# Revit family: Tub_Spout-American_Standard-Townsend_S-888809X_Series
name_source: partatom
category: Plumbing Fixtures
units: mm (PartAtom-declared; Revit-internal decimal feet)

## family parameters
Cut with Voids When Loaded = No
Host = Face
OmniClass Number = 23.45.05.14.21
OmniClass Title = Bathtubs
Part Type = Normal
Room Calculation Point = No
Round Connector Dimension = Use Diameter
Shared = Yes

## types (9) — shared parameters
Assembly Code = D2020300
CW Connection = No
CWFU = 3
Default Elevation = 25"
HW Connection = No
HWFU = 3
Height = 2 5/8"
Installation Type = Wall Mounted
Length = 6 1/2"
Manufacturer = American Standard
Product Documentation Link = https://americanstandard.box.com
Product Page URL = https://www.americanstandard-us.com
Tempered Water Connection = Yes
Tempered Water Connection Diameter = 1/2"
URL = https://www.americanstandard-us.com
Vent Connection = No
WFU = 4
Warranty Information = Limited Lifetime Warranty
Waste Connection = No
Width = 2 5/8"

## per-type parameters (varying)
| type | Description | Finish | Material |
| 8888093.002 | Townsend® 6-1/2-Inch Slip-On Diverter Tub Spout | Metal-American_Standard-002-Polished_Chrome | Metal-American_Standard-002-Polished_Chrome |
| 8888098.295 | Townsend® 6-1/2-Inch IPS Diverter Tub Spout | Metal-American Standard-295-Brushed Nickel | Metal-American Standard-295-Brushed Nickel |
| 8888098.013 | Townsend® 6-1/2-Inch IPS Diverter Tub Spout | Metal-American_Standard-013-Polished Nickel | Metal-American_Standard-013-Polished Nickel |
| 8888098.278 | Townsend® 6-1/2-Inch IPS Diverter Tub Spout | Metal-American_Standard-278-Legacy Bronze | Metal-American_Standard-278-Legacy Bronze |
| 8888093.013 | Townsend® 6-1/2-Inch Slip-On Diverter Tub Spout | Metal-American_Standard-013-Polished Nickel | Metal-American_Standard-013-Polished Nickel |
| 8888093.278 | Townsend® 6-1/2-Inch Slip-On Diverter Tub Spout | Metal-American_Standard-278-Legacy Bronze | Metal-American_Standard-278-Legacy Bronze |
| 8888093.243 | Townsend® 6-1/2-Inch Slip-On Diverter Tub Spout | Metal-American Standard-243-Matte Black | Metal-American Standard-243-Matte Black |
| 8888093.295 | Townsend® 6-1/2-Inch Slip-On Diverter Tub Spout | Metal-American Standard-295-Brushed Nickel | Metal-American Standard-295-Brushed Nickel |
| 8888098.002 | Townsend® 6-1/2-Inch IPS Diverter Tub Spout | Metal-American_Standard-002-Polished_Chrome | Metal-American_Standard-002-Polished_Chrome |

note: column(s) folded — value = type name in every type: Model

## geometry (parser evidence)
native form markers: Sweep x3
no freeform markers — native parametric forms only
